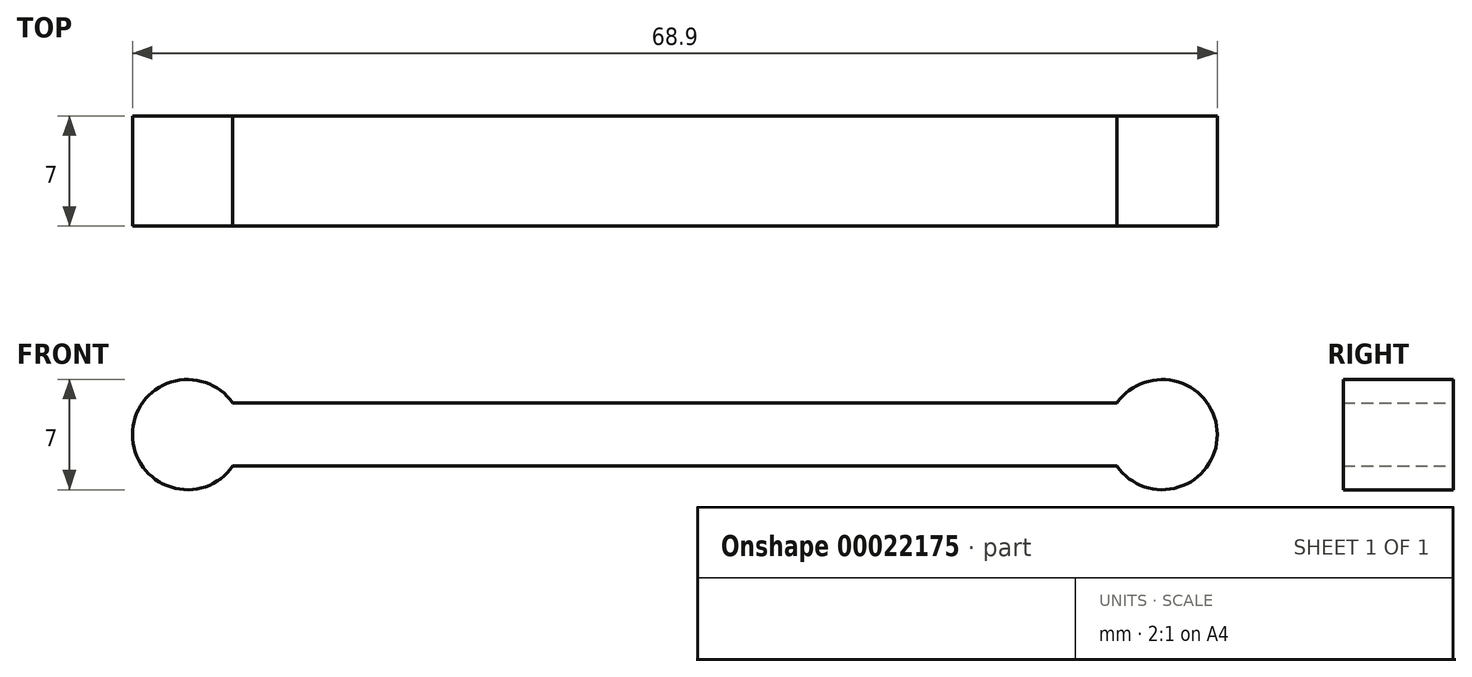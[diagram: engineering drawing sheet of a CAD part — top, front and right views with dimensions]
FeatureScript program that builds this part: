
annotation { "Feature Type Name" : "Feature", "Feature Type Description" : "" }
export const myFeature = defineFeature(function(context is Context, id is Id, definition is map)
    precondition{}
    {
        {
            var Q0;
            Q0=qCreatedBy(makeId("Front.planeOp"),FACE);
            var sketch = newSketch(context, id + "F0", { "sketchPlane" : qUnion([Q0])});
            skLineSegment(sketch, "E0.bottom", {"start": v(0, 0) * mm, "end": v(-61.9, 0) * mm});
            skLineSegment(sketch, "E0.top", {"start": v(0, 4) * mm, "end": v(-61.9, 4) * mm});
            skLineSegment(sketch, "E0.left", {"start": v(0, 0) * mm, "end": v(0, 4) * mm});
            skLineSegment(sketch, "E0.right", {"start": v(-61.9, 0) * mm, "end": v(-61.9, 4) * mm});
            skCircle(sketch, "E1", {"center": v(-61.9, 2) * mm, "radius": 3.5 * mm});
            skCircle(sketch, "E2", {"center": v(0, 2) * mm, "radius": 3.5 * mm});
            skSolve(sketch);
        }
        {
            var Q0;
            Q0=qSketchRegion(id+"F0",true);
            extrude(context, id + "F1", {"entities" : qUnion([Q0]), "depth" : 7 * mm});
        }
    });
